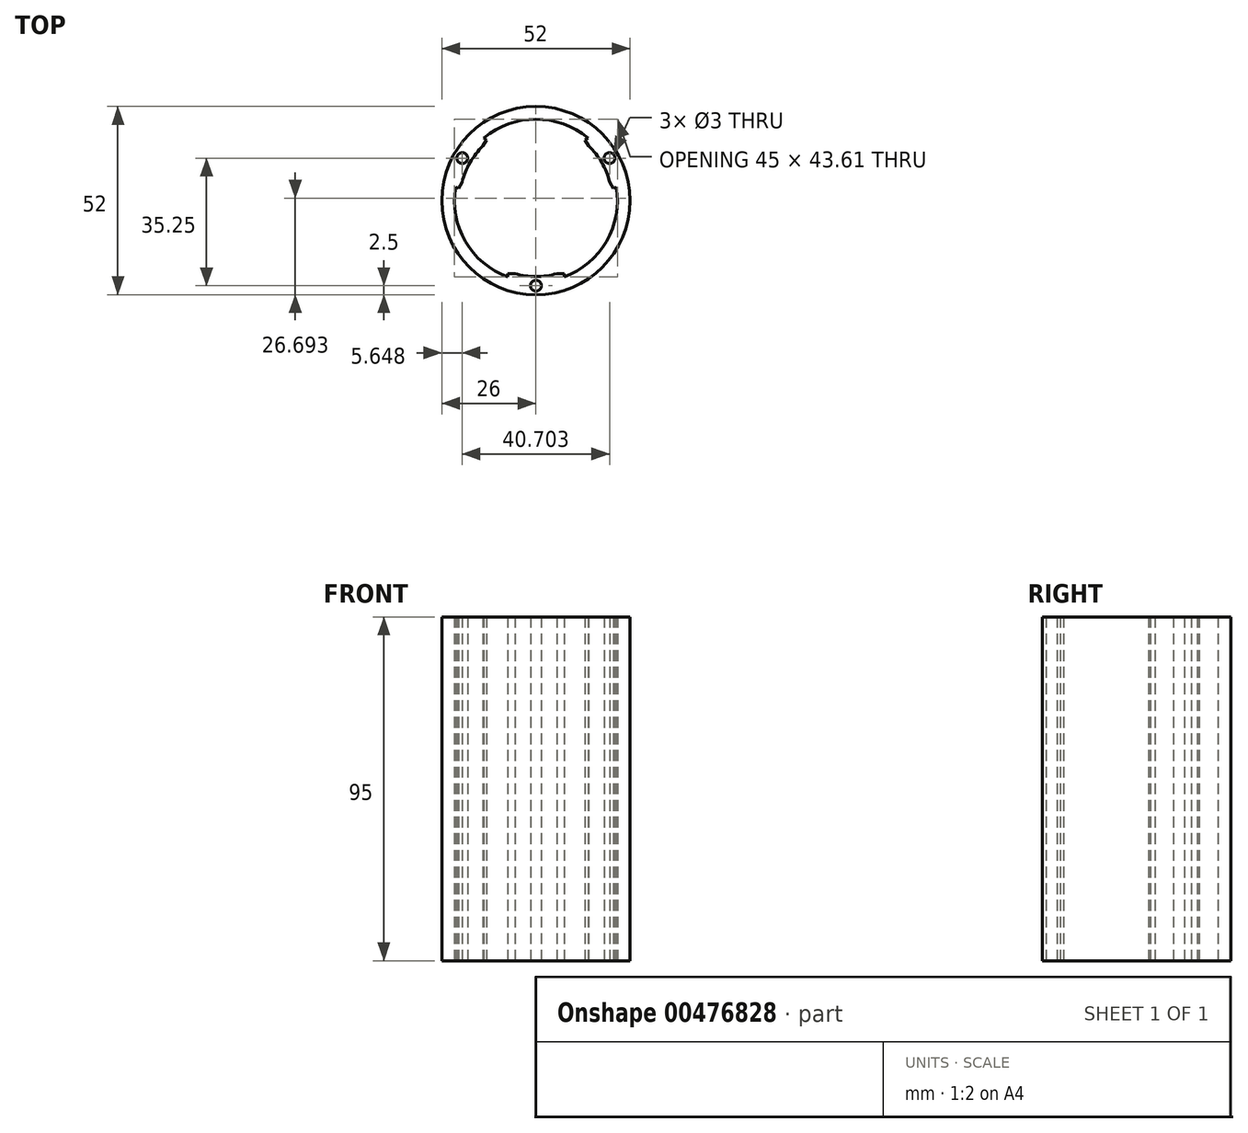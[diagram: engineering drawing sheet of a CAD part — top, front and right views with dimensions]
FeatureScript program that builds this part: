
annotation { "Feature Type Name" : "Feature", "Feature Type Description" : "" }
export const myFeature = defineFeature(function(context is Context, id is Id, definition is map)
    precondition{}
    {
        {
            var Q0;
            Q0=qCreatedBy(makeId("Top.planeOp"),FACE);
            var sketch = newSketch(context, id + "F0", { "sketchPlane" : qUnion([Q0])});
            skCircle(sketch, "E0", {"center": v(0, 0) * mm, "radius": 26 * mm});
            skCircle(sketch, "E1", {"center": v(0, 0) * mm, "radius": 21 * mm, "construction": true});
            skArc(sketch, "E2", {"start": v(7.77, -21.11) * mm, "mid": v(19.49, -11.25) * mm, "end": v(22.17, 3.82) * mm});
            skLineSegment(sketch, "E3.top", {"start": v(7.77, -20.19) * mm, "end": v(5.78, -20.19) * mm});
            skLineSegment(sketch, "E3.left", {"start": v(7.77, -21.11) * mm, "end": v(7.77, -20.19) * mm});
            skLineSegment(sketch, "E3.right", {"start": v(-7.77, -21.11) * mm, "end": v(-7.77, -20.19) * mm});
            skPoint(sketch, "E4", {"position": v(-5.78, -20.19) * mm});
            skPoint(sketch, "E5", {"position": v(5.78, -20.19) * mm});
            skFitSpline(sketch, "E6", {"points": [v(-5.78, -20.19) * mm, v(0, -21) * mm, v(5.78, -20.19) * mm], "startDerivative": vector(11.55, -2.43) * mm, "endDerivative": vector(11.55, 2.43) * mm});
            skLineSegment(sketch, "E7.trimOffspring", {"start": v(-5.78, -20.19) * mm, "end": v(-7.77, -20.19) * mm});
            skLineSegment(sketch, "E8.1.0", {"start": v(14.4, 17.3) * mm, "end": v(13.6, 16.83) * mm});
            skLineSegment(sketch, "E8.1.1", {"start": v(20.37, 5.1) * mm, "end": v(21.37, 3.36) * mm});
            skLineSegment(sketch, "E8.1.2", {"start": v(13.6, 16.83) * mm, "end": v(14.6, 15.1) * mm});
            skLineSegment(sketch, "E8.1.3", {"start": v(22.17, 3.82) * mm, "end": v(21.37, 3.36) * mm});
            skLineSegment(sketch, "E8.2.0", {"start": v(-22.17, 3.82) * mm, "end": v(-21.37, 3.36) * mm});
            skLineSegment(sketch, "E8.2.1", {"start": v(-14.6, 15.1) * mm, "end": v(-13.6, 16.83) * mm});
            skLineSegment(sketch, "E8.2.2", {"start": v(-21.37, 3.36) * mm, "end": v(-20.37, 5.1) * mm});
            skLineSegment(sketch, "E8.2.3", {"start": v(-14.4, 17.3) * mm, "end": v(-13.6, 16.83) * mm});
            skArc(sketch, "E9", {"start": v(-14.6, 15.1) * mm, "mid": v(-18.19, 10.5) * mm, "end": v(-20.37, 5.1) * mm});
            skArc(sketch, "E10", {"start": v(20.37, 5.1) * mm, "mid": v(18.2, 10.5) * mm, "end": v(14.6, 15.1) * mm});
            skArc(sketch, "E11", {"start": v(-5.78, -20.19) * mm, "mid": v(0, -21) * mm, "end": v(5.78, -20.19) * mm});
            skArc(sketch, "E12.trimOffspring", {"start": v(14.4, 17.3) * mm, "mid": v(0, 22.5) * mm, "end": v(-14.4, 17.3) * mm});
            skArc(sketch, "E13.trimOffspring", {"start": v(-22.17, 3.82) * mm, "mid": v(-19.49, -11.25) * mm, "end": v(-7.77, -21.11) * mm});
            skCircle(sketch, "E14", {"center": v(0, -23.5) * mm, "radius": 1.5 * mm});
            skCircle(sketch, "E15.1.0", {"center": v(20.35, 11.75) * mm, "radius": 1.5 * mm});
            skCircle(sketch, "E15.2.0", {"center": v(-20.35, 11.75) * mm, "radius": 1.5 * mm});
            skSolve(sketch);
        }
        {
            var Q0;
            Q0=makeQuery(id+"F0.imprint","IMPRINT",FACE,{"disambiguationData":[TD([[makeQuery(id+"F0.imprint","IMPRINT",EDGE,{"derivedFrom":sQuery(id+"F0.wireOp",EDGE,"E0")}),1.0]])]});
            extrude(context, id + "F1", {"entities" : qUnion([Q0]), "depth" : 95 * mm});
        }
    });
